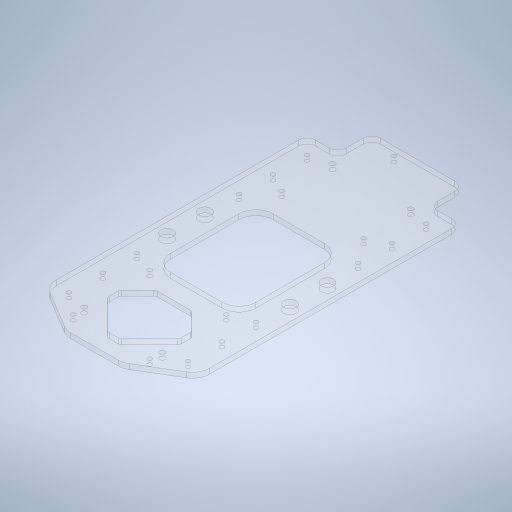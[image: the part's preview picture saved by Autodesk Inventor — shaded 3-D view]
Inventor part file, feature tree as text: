
AUTODESK INVENTOR PART (.ipt)
format: ipt  version: 2023 (Build 270158000, 158)  size: 441,856 bytes
history: native  units: in
note: dims shown in document units (in); Inventor stores cm internally (conversion verified against a paired STEP export)
features: extrude x1
ambient origin geometry x8: Origin, YZ Plane, XZ Plane, XY Plane, X Axis, Y Axis, Z Axis, Center Point
bodies: Body1 (feature_tree)
feature tree (1):
  extrude  "Extrusion2"  Depth=3.5433in
